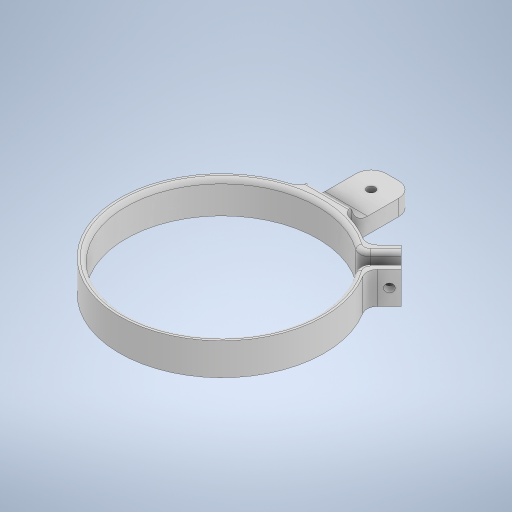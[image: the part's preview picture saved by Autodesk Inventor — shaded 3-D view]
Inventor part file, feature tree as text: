
AUTODESK INVENTOR PART (.ipt)
format: ipt  version: 2024.2 (Build 282272000, 272)  size: 345,600 bytes
history: native  units: mm
features: fillet x4, extrude x3, sketch x3
ambient origin geometry x8: Origin, YZ Plane, XZ Plane, XY Plane, X Axis, Y Axis, Z Axis, Center Point
bodies: Solid1 (feature_tree)
feature tree (10):
  extrude  "Extrusion1"  Depth=90.0mm
  fillet  "Fillet1"  Radius=20.0mm
  extrude  "Extrusion3"  Depth=4.0mm
  fillet  "Fillet2"  Radius=4.0mm
  extrude  "Extrusion4"  Depth=7.0mm
  fillet  "Fillet3"  Radius=7.0mm
  fillet  "Fillet4"  Radius=15.0mm
  sketch  "Sketch1"  dims[d0=96.0mm d1=90.0mm d2=20.0mm]
  sketch  "Sketch5"  dims[d6=15.0mm d7=0.0mm d13=35.0mm d14=4.0mm]
  sketch  "Sketch6"  dims[d15=45.0deg d16=7.0mm d17=7.0mm d18=15.0mm d19=3.0mm d20=3.0mm d21=5.0mm d22=0.0mm d23=0.0mm d24=7.0mm d25=4.0mm d26=10.0mm d27=0.0mm d28=2.0mm d29=2.0mm]
